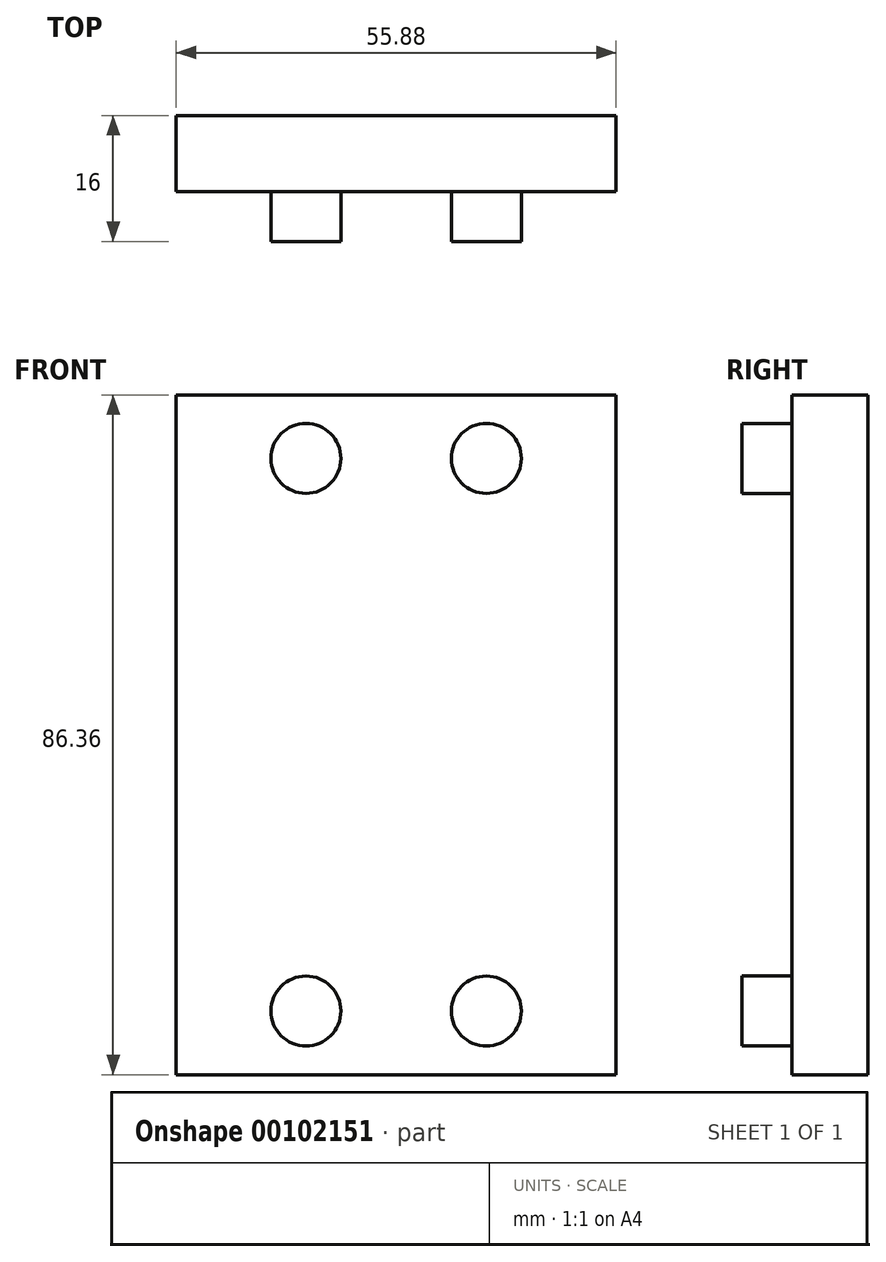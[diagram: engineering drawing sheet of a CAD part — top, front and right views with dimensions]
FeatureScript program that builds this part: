
annotation { "Feature Type Name" : "Feature", "Feature Type Description" : "" }
export const myFeature = defineFeature(function(context is Context, id is Id, definition is map)
    precondition{}
    {
        {
            var Q0;
            Q0=qCreatedBy(makeId("Front.planeOp"),FACE);
            var sketch = newSketch(context, id + "F0", { "sketchPlane" : qUnion([Q0])});
            skLineSegment(sketch, "E0.bottom", {"start": v(-54.9, 95.66) * mm, "end": v(0.99, 95.66) * mm});
            skLineSegment(sketch, "E0.top", {"start": v(-54.9, 9.3) * mm, "end": v(0.99, 9.3) * mm});
            skLineSegment(sketch, "E0.left", {"start": v(-54.9, 95.66) * mm, "end": v(-54.9, 9.3) * mm});
            skLineSegment(sketch, "E0.right", {"start": v(0.99, 95.66) * mm, "end": v(0.99, 9.3) * mm});
            skSolve(sketch);
        }
        {
            var Q0;
            Q0 = qSketchRegion(id + "F0", true);
            extrude(context, id + "F1", {"entities" : qUnion([Q0]), "depth" : 9.65 * mm});
        }
        {
            var Q0;
            Q0=makeQuery(id+"F1.opExtrude","CAP_FACE",FACE,{"disambiguationData":[OSD([sQuery(id+"F0.wireOp",EDGE,"E0.bottom"),sQuery(id+"F0.wireOp",EDGE,"E0.top"),sQuery(id+"F0.wireOp",EDGE,"E0.left"),sQuery(id+"F0.wireOp",EDGE,"E0.right")])],"isStart":false});
            var sketch = newSketch(context, id + "F2", { "sketchPlane" : qUnion([Q0])});
            skCircle(sketch, "E1", {"center": v(-38.41, 87.59) * mm, "radius": 4.45 * mm});
            skCircle(sketch, "E2", {"center": v(-15.5, 87.59) * mm, "radius": 4.45 * mm});
            skCircle(sketch, "E3", {"center": v(-38.41, 17.38) * mm, "radius": 4.45 * mm});
            skCircle(sketch, "E4", {"center": v(-15.5, 17.38) * mm, "radius": 4.45 * mm});
            skSolve(sketch);
        }
        {
            var Q0;
            Q0 = qSketchRegion(id + "F2", true);
            extrude(context, id + "F3", {"entities" : qUnion([Q0]), "operationType" : NewBodyOperationType.ADD, "depth" : 6.35 * mm});
        }
    });
